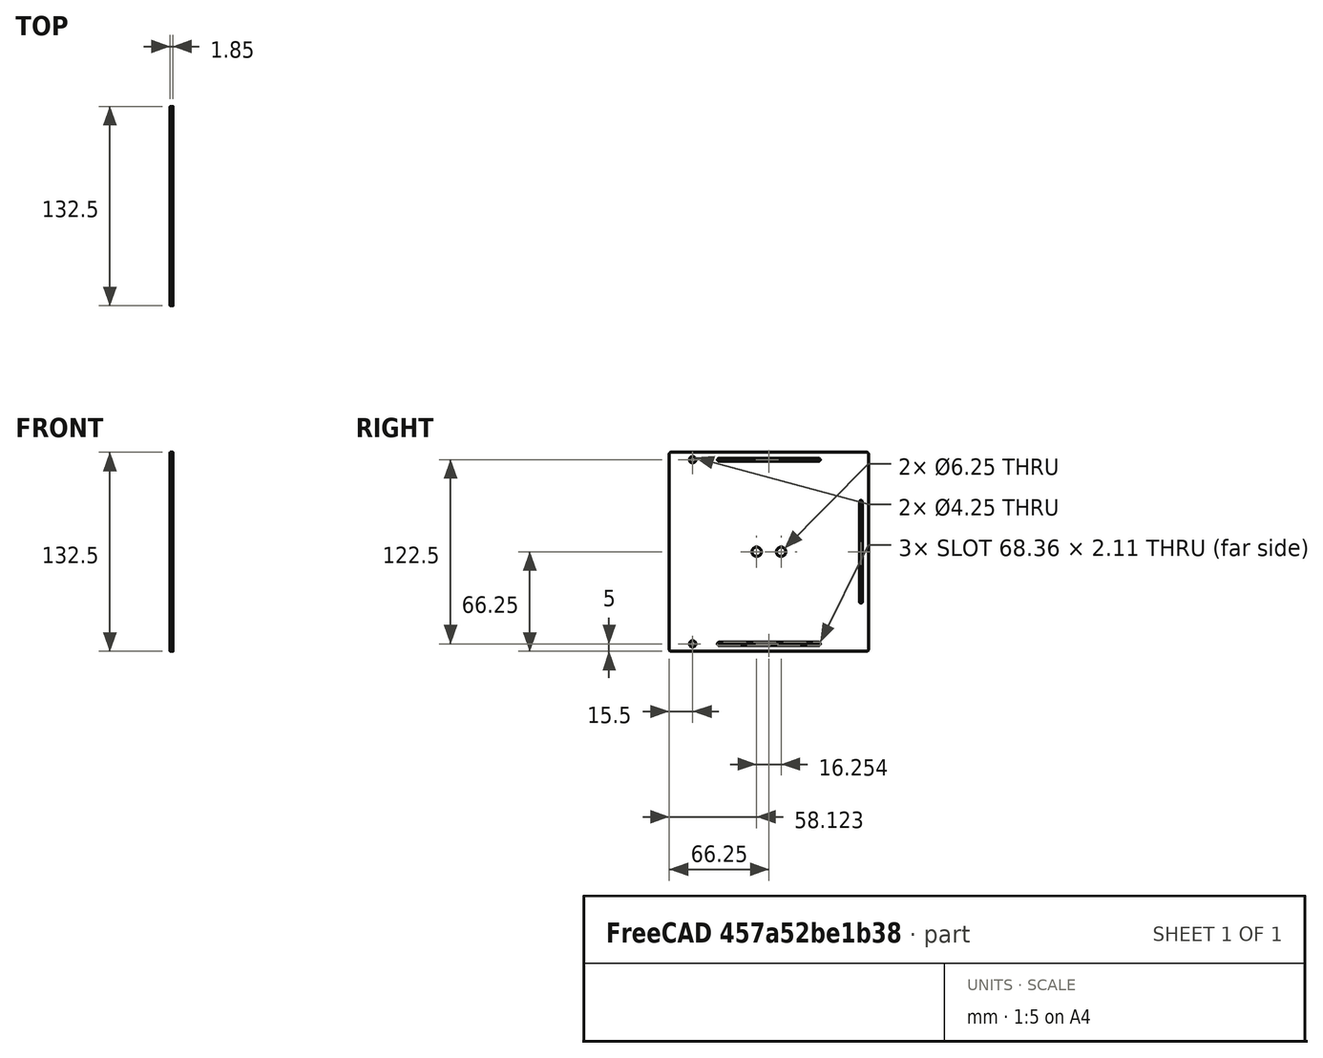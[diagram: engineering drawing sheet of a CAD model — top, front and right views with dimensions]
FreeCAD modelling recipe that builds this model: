
FCSTD DOCUMENT  (FreeCAD 1.0R38641 +468 (Git))
Label: panel_side
License: All rights reserved
LicenseURL: https://en.wikipedia.org/wiki/All_rights_reserved
objects: PartDesign::SubShapeBinder×1, Sketcher::SketchObject×1, PartDesign::Pad×1, PartDesign::Body×1
note: 7 computed .brp shape members not serialized (recipe doc carries the construction recipe); baked Part::Feature solids carry a one-line shape summary decoded from their .brp
EXTERNAL_REF file=dimensions.FCStd obj=VarSet
EXTERNAL_REF file=../third_party/tiptop_z_rail.FCStd obj=Body

FEATURE [PartDesign::SubShapeBinder] Binder001  label="RailBinder"
  BindCopyOnChange = 0
  BindMode = 0
  ClaimChildren = false
  Context = -> Body001 [Binder001.]
  Fuse = false
  MakeFace = true
  OffsetFill = false
  OffsetIntersection = false
  OffsetJoinType = 0
  OffsetOpenResult = false
  PartialLoad = false
  Refine = true
  Relative = true
  Support = -> [<external ../third_party/tiptop_z_rail.FCStd>#Body]
  _Version = 2
FEATURE [Sketcher::SketchObject] Sketch
  ArcFitTolerance = 1e-06
  AttachmentSupport = -> [Binder001]
  ExternalGeometry = -> [Binder001]
  FullyConstrained = true
  MakeInternals = false
  MapMode = 5
  Placement = pos=(1e-15,0,0) rot=(0.57735,0.57735,0.57735;2.0944rad)
  expr: .Constraints.CornerRadius = <<dimensions>>#VarSet.EnclosureCornerRadius
  expr: .Constraints.MaxBoltNutOuterDiameter = dimensions#VarSet.EnclosureFrameHoleDiameter + dimensions#VarSet.FrameMinWidth + 2 * dimensions#VarSet.FrameFinishThickness
  expr: Constraints[21] = <<dimensions>>#VarSet.EnclosureFrameHoleDiameter
  expr: Constraints[61] = 122.5
  expr: Constraints[63] = <<dimensions>>#VarSet.EnclosureTotalThickness + 2 * <<dimensions>>#VarSet.EnclosureFinishThickness
  expr: Constraints[71] = <<dimensions>>#VarSet.EnclosureRailHoleDiameter
  sketch-geometry (32):
    g0: LineSegment [constr] StartX=-1.2 StartY=-56.25 StartZ=0 EndX=131.3 EndY=-56.25 EndZ=0
    g1: Circle CenterX=14.3 CenterY=5 CenterZ=0 NormalX=0 NormalY=0 NormalZ=1 AngleXU=0 Radius=2.127
    g2: Circle CenterX=14.3 CenterY=-117.5 CenterZ=0 NormalX=0 NormalY=0 NormalZ=1 AngleXU=0 Radius=2.127
    g3: LineSegment [constr] StartX=14.3 StartY=5 StartZ=0 EndX=31.925 EndY=5 EndZ=0
    g4: LineSegment StartX=31.925 StartY=3.9459 StartZ=0 EndX=98.175 EndY=3.9459 EndZ=0
    g5: LineSegment StartX=98.175 StartY=6.0541 StartZ=0 EndX=31.925 EndY=6.0541 EndZ=0
    g6: LineSegment [constr] StartX=65.05 StartY=10 StartZ=0 EndX=65.05 EndY=-122.5 EndZ=0
    g7: LineSegment StartX=4.7e-14 StartY=10 StartZ=0 EndX=130.1 EndY=10 EndZ=0
    g8: ArcOfCircle CenterX=4.69e-14 CenterY=8.8 CenterZ=0 NormalX=0 NormalY=0 NormalZ=1 AngleXU=0 Radius=1.2 StartAngle=1.5708 EndAngle=3.14159
    g9: ArcOfCircle CenterX=130.1 CenterY=8.8 CenterZ=0 NormalX=0 NormalY=0 NormalZ=1 AngleXU=0 Radius=1.2 StartAngle=-9e-16 EndAngle=1.5708
    g10: LineSegment StartX=131.3 StartY=8.8 StartZ=0 EndX=131.3 EndY=-121.3 EndZ=0
    g11: LineSegment StartX=-1.2 StartY=8.8 StartZ=0 EndX=-1.2 EndY=-121.3 EndZ=0
    g12: LineSegment StartX=4.65e-14 StartY=-122.5 StartZ=0 EndX=130.1 EndY=-122.5 EndZ=0
    g13: ArcOfCircle CenterX=4.67e-14 CenterY=-121.3 CenterZ=0 NormalX=0 NormalY=0 NormalZ=1 AngleXU=0 Radius=1.2 StartAngle=3.14159 EndAngle=4.71239
    g14: ArcOfCircle CenterX=130.1 CenterY=-121.3 CenterZ=0 NormalX=0 NormalY=0 NormalZ=1 AngleXU=0 Radius=1.2 StartAngle=4.71239 EndAngle=6.28319
    g15: LineSegment [constr] StartX=31.925 StartY=6.0541 StartZ=0 EndX=31.925 EndY=10 EndZ=0
    g16: Circle CenterX=56.923 CenterY=-56.25 CenterZ=0 NormalX=0 NormalY=0 NormalZ=1 AngleXU=0 Radius=3.127
    g17: Circle CenterX=73.177 CenterY=-56.25 CenterZ=0 NormalX=0 NormalY=0 NormalZ=1 AngleXU=0 Radius=3.127
    g18: Circle [constr] CenterX=56.923 CenterY=-56.25 CenterZ=0 NormalX=0 NormalY=0 NormalZ=1 AngleXU=0 Radius=8.127
    g19: ArcOfCircle CenterX=31.925 CenterY=5 CenterZ=0 NormalX=0 NormalY=0 NormalZ=1 AngleXU=0 Radius=1.0541 StartAngle=1.5708 EndAngle=4.71239
    g20: ArcOfCircle CenterX=98.175 CenterY=5 CenterZ=0 NormalX=0 NormalY=0 NormalZ=1 AngleXU=0 Radius=1.0541 StartAngle=4.71239 EndAngle=7.85398
    g21: ArcOfCircle CenterX=126.3 CenterY=-23.125 CenterZ=0 NormalX=0 NormalY=0 NormalZ=1 AngleXU=0 Radius=1.0541 StartAngle=-9e-16 EndAngle=3.14159
    g22: ArcOfCircle CenterX=126.3 CenterY=-89.375 CenterZ=0 NormalX=0 NormalY=0 NormalZ=1 AngleXU=0 Radius=1.0541 StartAngle=3.14159 EndAngle=6.28319
    g23: LineSegment StartX=127.354 StartY=-23.125 StartZ=0 EndX=127.354 EndY=-89.375 EndZ=0
    g24: LineSegment StartX=125.246 StartY=-23.125 StartZ=0 EndX=125.246 EndY=-89.375 EndZ=0
    g25: LineSegment [constr] StartX=127.354 StartY=-23.125 StartZ=0 EndX=131.3 EndY=-23.125 EndZ=0
    g26: LineSegment [constr] StartX=31.925 StartY=-122.5 StartZ=0 EndX=31.925 EndY=-118.554 EndZ=0
    g27: ArcOfCircle CenterX=31.925 CenterY=-117.5 CenterZ=0 NormalX=0 NormalY=0 NormalZ=1 AngleXU=0 Radius=1.0541 StartAngle=1.5708 EndAngle=4.71239
    g28: ArcOfCircle CenterX=98.175 CenterY=-117.5 CenterZ=0 NormalX=0 NormalY=0 NormalZ=1 AngleXU=0 Radius=1.0541 StartAngle=4.71239 EndAngle=7.85398
    g29: LineSegment StartX=31.925 StartY=-116.446 StartZ=0 EndX=98.175 EndY=-116.446 EndZ=0
    g30: LineSegment StartX=31.925 StartY=-118.554 StartZ=0 EndX=98.175 EndY=-118.554 EndZ=0
    g31: LineSegment [constr] StartX=-1.2 StartY=3.9459 StartZ=0 EndX=65.05 EndY=3.9459 EndZ=0
  constraints (76):
    c: Symmetric(g2,g1,g0)
    c: Equal(g1,g2)
    c: Coincident(g3,g1)
    c: Horizontal(g3)
    c: Equal(g8,g9)
    c: Tangent(g9,g10) = 1.5708
    c: Tangent(g7,g9) = 1.5708
    c: Tangent(g13,g11) = -1.5708
    c: Tangent(g13,g12) = -1.5708
    c: Equal(g13,g8)
    c: Tangent(g12,g14) = -1.5708
    c: Tangent(g14,g10) = 1.5708
    c: Equal(g14,g8)
    c: Vertical(g15)
    c: Symmetric(g4,g4,g6)
    c: Horizontal(g5)
    c: Horizontal(g7)
    c: PointOnObject(g16,g0)
    c: PointOnObject(g17,g0)
    c: Equal(g16,g17)
    c: Symmetric(g16,g17,g6)
    c: Diameter(g17) = 6.254
    c: Coincident(g18,g16)
    c: Tangent(g18,g6)
    c: Diameter(g18) = 16.254  'MaxBoltNutOuterDiameter'
    c: Coincident(g19,g3)
    c: Tangent(g5,g19) = -1.5708
    c: Tangent(g4,g19) = -1.5708
    c: Tangent(g5,g20) = -1.5708
    c: Tangent(g4,g20) = -1.5708
    c: Tangent(g21,g23) = 1.5708
    c: Tangent(g21,g24) = -1.5708
    c: Tangent(g22,g23) = 1.5708
    c: Tangent(g22,g24) = -1.5708
    c: Equal(g21,g22)
    c: Symmetric(g22,g21,g0)
    c: Coincident(g15,g5)
    c: Coincident(g25,g21)
    c: Horizontal(g25)
    c: PointOnObject(g25,g10)
    c: Equal(g25,g15)
    c: PointOnObject(g26,g12)
    c: Vertical(g26)
    c: Tangent(g27,g29) = 1.5708
    c: Tangent(g27,g30) = -1.5708
    c: Tangent(g28,g29) = 1.5708
    c: Tangent(g28,g30) = -1.5708
    c: Equal(g27,g28)
    c: Coincident(g26,g27)
    c: Equal(g26,g15)
    c: Equal(g27,g19)
    c: Symmetric(g27,g28,g6)
    c: Vertical(g11)
    c: Tangent(g8,g11) = -1.5708
    c: Tangent(g7,g8) = 1.5708
    c: Symmetric(g8,g11,g0)
    c: Symmetric(g9,g10,g0)
    c: Symmetric(g12,g12,g6)
    c: Symmetric(g7,g7,g6)
    c: Equal(g4,g24)
    c: Equal(g4,g29)
    c: DistanceY(g2,g1) = 122.5
    c: Equal(g7,g11)
    c: Distance(g21,g21) = 2.1082
    c: PointOnObject(g15,g7)
    c: PointOnObject(g31,g11)
    c: Symmetric(g4,g4,g31)
    c: Symmetric(g31,g31,g4)
    c: Radius(g13) = 1.2  'CornerRadius'
    c: Distance(g15,g15) = 3.9459  'EdgeToSlot'
    c: DistanceX(g5,g5) = 66.25  'SlotLength'
    c: Diameter(g1) = 4.254
    c: Equal(g20,g21)
    c: Horizontal(g12)
    c: Coincident(g1,g-3)
    c: Coincident(g-4,g7)
FEATURE [PartDesign::Pad] Pad
  Direction = (1,0,0)
  Length = 1.8542
  Length2 = 10
  Profile = -> Sketch
  ReferenceAxis = -> Sketch [N_Axis]
  Refine = true
  Reversed = true
  Suppressed = false
  Type = 0
  expr: Length = <<dimensions>>#VarSet.EnclosureTotalThickness
FEATURE [PartDesign::Body] Body001  label="PanelSide"
  AllowCompound = false
  Group = -> [Sketch,Pad,Binder001]
  Origin = -> Origin001
  Tip = -> Pad
